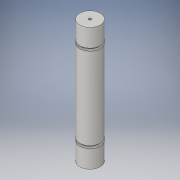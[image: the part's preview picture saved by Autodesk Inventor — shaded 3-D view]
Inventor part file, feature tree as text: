
AUTODESK INVENTOR PART (.ipt)
format: ipt  version: 2016 (Build 200138000, 138)  size: 134,144 bytes
history: native  units: in
note: dims shown in document units (in); Inventor stores cm internally (conversion verified against a paired STEP export)
features: sketch x2, revolve x1, hole x1
ambient origin geometry x8: Origin, YZ Plane, XZ Plane, XY Plane, X Axis, Y Axis, Z Axis, Center Point
bodies: Solid1 (feature_tree)
feature tree (4):
  revolve  "Revolution1"  [1 undecoded]
  hole  "Hole1"  [1 undecoded]
  sketch  "Sketch1"  dims[d2=90.0deg d3=0.25in]
  sketch  "Sketch2"  dims[d4=0.25in d5=0.25in d7=0.25in d8=1.0in d9=1.0in d10=1.0in d11=12.0in d12=6.0in d13=4.0in d14=4.0in d15=0.26in d16=0.75in d17=0.375in d18=0.25in d19=0.5635in d20=1.0in d21=0.8108in]
note: 2 required parameter values undecoded (feature->parameter linkage not recoverable at this tier; creation-order binding heuristic only, values carry confidence <= 0.55)